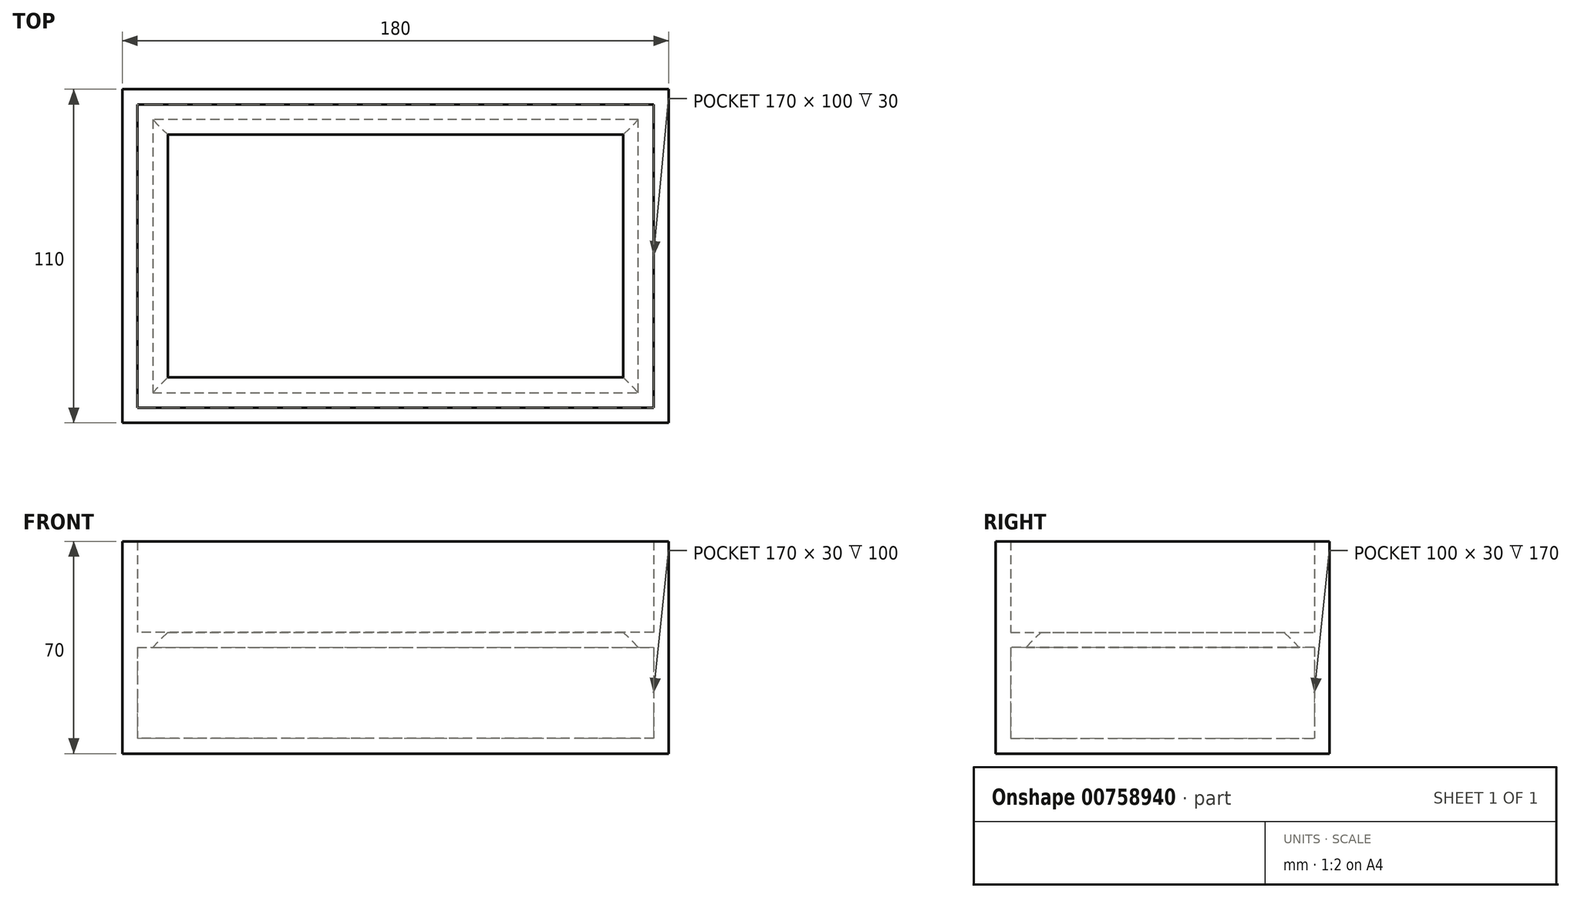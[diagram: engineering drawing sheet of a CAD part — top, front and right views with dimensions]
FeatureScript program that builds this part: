
annotation { "Feature Type Name" : "Feature", "Feature Type Description" : "" }
export const myFeature = defineFeature(function(context is Context, id is Id, definition is map)
    precondition{}
    {
        {
            var Q0;
            Q0=qCreatedBy(makeId("Top.planeOp"),FACE);
            var sketch = newSketch(context, id + "F0", { "sketchPlane" : qUnion([Q0])});
            skLineSegment(sketch, "E0.bottom", {"start": v(90, -55) * mm, "end": v(-90, -55) * mm});
            skLineSegment(sketch, "E0.top", {"start": v(90, 55) * mm, "end": v(-90, 55) * mm});
            skLineSegment(sketch, "E0.left", {"start": v(90, -55) * mm, "end": v(90, 55) * mm});
            skLineSegment(sketch, "E0.right", {"start": v(-90, -55) * mm, "end": v(-90, 55) * mm});
            skPoint(sketch, "E0.middle", {"position": v(0, 0) * mm});
            skSolve(sketch);
        }
        {
            var Q0;
            Q0=makeQuery(id+"F0.imprint","IMPRINT",FACE,{"disambiguationData":[TD([[makeQuery(id+"F0.imprint","IMPRINT",EDGE,{"derivedFrom":sQuery(id+"F0.wireOp",EDGE,"E0.bottom")}),-1.0]])]});
            var sketch = newSketch(context, id + "F1", { "sketchPlane" : qUnion([Q0])});
            skLineSegment(sketch, "E1.bottom", {"start": v(85, -50) * mm, "end": v(-85, -50) * mm});
            skLineSegment(sketch, "E1.top", {"start": v(85, 50) * mm, "end": v(-85, 50) * mm});
            skLineSegment(sketch, "E1.left", {"start": v(85, -50) * mm, "end": v(85, 50) * mm});
            skLineSegment(sketch, "E1.right", {"start": v(-85, -50) * mm, "end": v(-85, 50) * mm});
            skPoint(sketch, "E1.middle", {"position": v(0, 0) * mm});
            skSolve(sketch);
        }
        {
            var Q0;
            Q0=makeQuery(id+"F1.imprint","IMPRINT",FACE,{"disambiguationData":[TD([[makeQuery(id+"F1.imprint","IMPRINT",EDGE,{"derivedFrom":sQuery(id+"F1.wireOp",EDGE,"E1.bottom")}),1.0]])]});
            extrude(context, id + "F2", {"entities" : qUnion([Q0]), "depth" : 70 * mm, "offsetDistance" : 25 * mm});
        }
        {
            var Q0;
            Q0=makeQuery(id+"F0.imprint","IMPRINT",FACE,{"disambiguationData":[TD([[makeQuery(id+"F0.imprint","IMPRINT",EDGE,{"derivedFrom":sQuery(id+"F0.wireOp",EDGE,"E0.bottom")}),-1.0]])]});
            extrude(context, id + "F3", {"entities" : qUnion([Q0]), "operationType" : NewBodyOperationType.ADD, "depth" : 5 * mm, "offsetDistance" : 25 * mm});
        }
        {
            var Q0;
            Q0=qCreatedBy(makeId("Top.planeOp"),FACE);
            cPlane(context, id + "F4", {"entities" : qUnion([Q0]), "cplaneType" : CPlaneType.OFFSET, "offset" : 35 * mm, "width" : 150 * mm, "height" : 150 * mm});
        }
        {
            var Q0;
            Q0=qCreatedBy(id+"F4.planeOp",FACE);
            var sketch = newSketch(context, id + "F5", { "sketchPlane" : qUnion([Q0])});
            skLineSegment(sketch, "E2.bottom", {"start": v(-85, 50) * mm, "end": v(85, 50) * mm});
            skLineSegment(sketch, "E2.top", {"start": v(-85, -50) * mm, "end": v(85, -50) * mm});
            skLineSegment(sketch, "E2.left", {"start": v(-85, 50) * mm, "end": v(-85, -50) * mm});
            skLineSegment(sketch, "E2.right", {"start": v(85, 50) * mm, "end": v(85, -50) * mm});
            skPoint(sketch, "E2.middle", {"position": v(0, 0) * mm});
            skLineSegment(sketch, "E3.bottom", {"start": v(80, -45) * mm, "end": v(-80, -45) * mm});
            skLineSegment(sketch, "E3.top", {"start": v(80, 45) * mm, "end": v(-80, 45) * mm});
            skLineSegment(sketch, "E3.left", {"start": v(80, -45) * mm, "end": v(80, 45) * mm});
            skLineSegment(sketch, "E3.right", {"start": v(-80, -45) * mm, "end": v(-80, 45) * mm});
            skSolve(sketch);
        }
        {
            var Q0;
            Q0=makeQuery(id+"F5.imprint","IMPRINT",FACE,{"disambiguationData":[TD([[makeQuery(id+"F5.imprint","IMPRINT",EDGE,{"derivedFrom":sQuery(id+"F5.wireOp",EDGE,"E2.bottom")}),-1.0]])]});
            extrude(context, id + "F6", {"entities" : qUnion([Q0]), "operationType" : NewBodyOperationType.ADD, "depth" : 5 * mm, "offsetDistance" : 25 * mm, "hasDraft" : true, "draftAngle" : 45 * degree});
        }
    });
